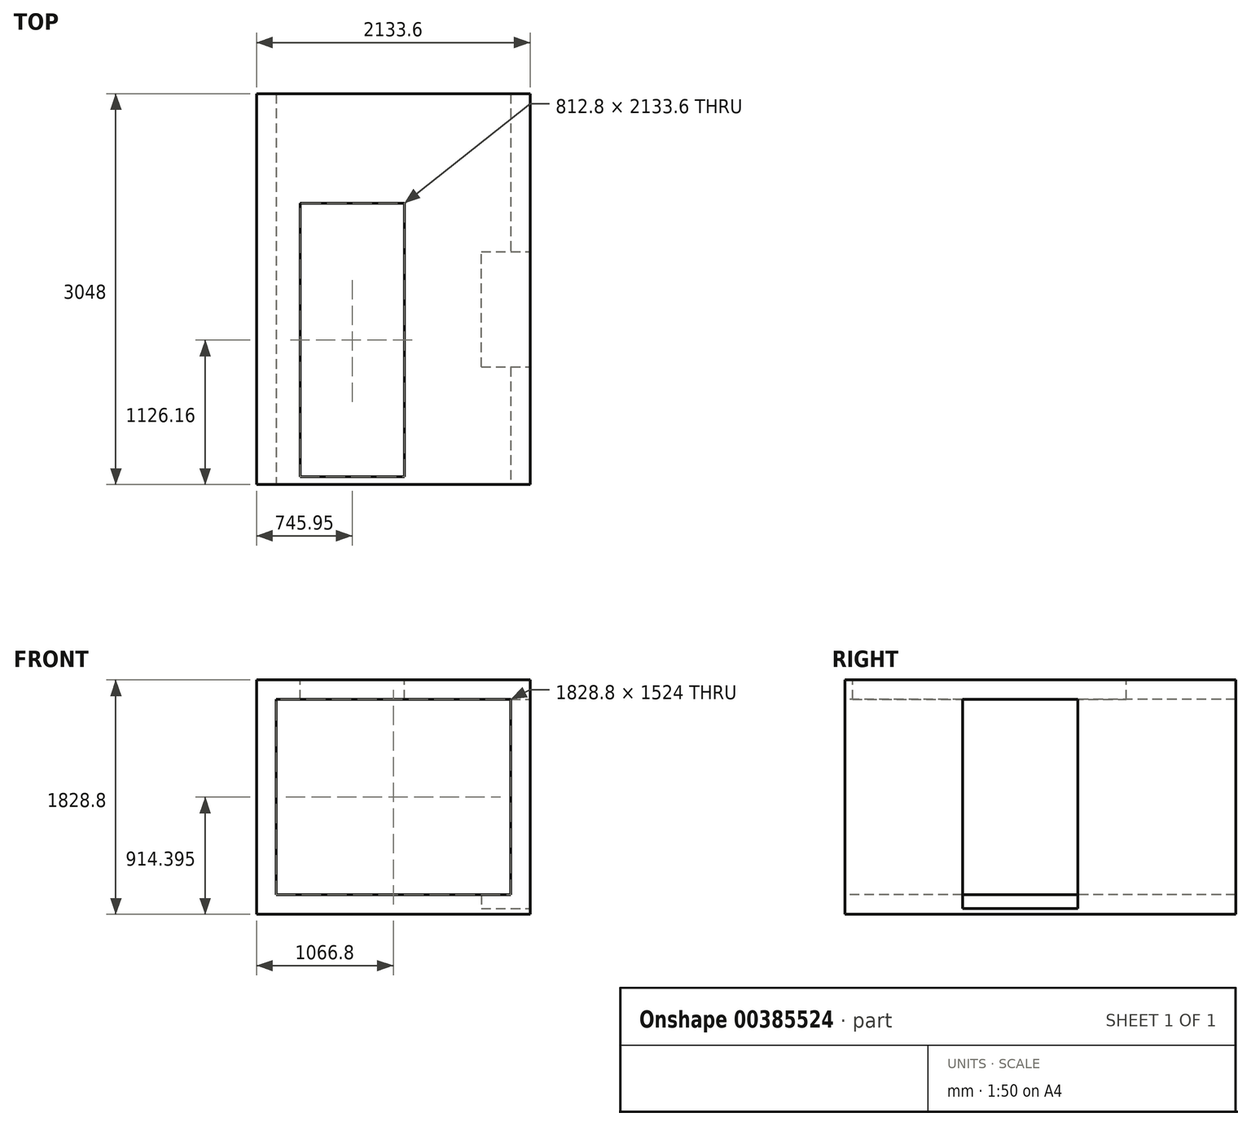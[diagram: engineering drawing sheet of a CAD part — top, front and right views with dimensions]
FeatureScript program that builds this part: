
annotation { "Feature Type Name" : "Feature", "Feature Type Description" : "" }
export const myFeature = defineFeature(function(context is Context, id is Id, definition is map)
    precondition{}
    {
        {
            var Q0;
            Q0=qCreatedBy(makeId("Front.planeOp"),FACE);
            var sketch = newSketch(context, id + "F0", { "sketchPlane" : qUnion([Q0])});
            skLineSegment(sketch, "E0.bottom", {"start": v(1794.05, -42.21) * mm, "end": v(-339.55, -42.21) * mm});
            skLineSegment(sketch, "E0.top", {"start": v(1794.05, 1786.59) * mm, "end": v(-339.55, 1786.59) * mm});
            skLineSegment(sketch, "E0.left", {"start": v(1794.05, -42.21) * mm, "end": v(1794.05, 1786.59) * mm});
            skLineSegment(sketch, "E0.right", {"start": v(-339.55, -42.21) * mm, "end": v(-339.55, 1786.59) * mm});
            skPoint(sketch, "E0.middle", {"position": v(727.25, 872.19) * mm});
            skSolve(sketch);
        }
        {
            var Q0;
            Q0 = qSketchRegion(id + "F0", true);
            extrude(context, id + "F1", {"entities" : qUnion([Q0]), "depth" : 3048 * mm});
        }
        {
            var Q0;
            Q0=makeQuery(id+"F1.opExtrude","CAP_FACE",FACE,{"disambiguationData":[OSD([sQuery(id+"F0.wireOp",EDGE,"E0.bottom"),sQuery(id+"F0.wireOp",EDGE,"E0.top"),sQuery(id+"F0.wireOp",EDGE,"E0.left"),sQuery(id+"F0.wireOp",EDGE,"E0.right")])],"isStart":false});
            var sketch = newSketch(context, id + "F2", { "sketchPlane" : qUnion([Q0])});
            skLineSegment(sketch, "E1.0", {"start": v(1641.65, 110.19) * mm, "end": v(1641.65, 1634.19) * mm});
            skLineSegment(sketch, "E1.1", {"start": v(-187.15, 110.19) * mm, "end": v(1641.65, 110.19) * mm});
            skLineSegment(sketch, "E1.2", {"start": v(-187.15, 1634.19) * mm, "end": v(-187.15, 110.19) * mm});
            skLineSegment(sketch, "E1.3", {"start": v(1641.65, 1634.19) * mm, "end": v(-187.15, 1634.19) * mm});
            skSolve(sketch);
        }
        {
            var Q0;
            Q0 = qSketchRegion(id + "F2", true);
            extrude(context, id + "F3", {"entities" : qUnion([Q0]), "operationType" : NewBodyOperationType.REMOVE, "oppositeDirection" : true, "depth" : 3302 * mm});
        }
        {
            var Q0;
            Q0=makeQuery(id+"F1.opExtrude","SWEPT_FACE",FACE,{"disambiguationData":[OSD([sQuery(id+"F0.wireOp",EDGE,"E0.top")])]});
            var sketch = newSketch(context, id + "F4", { "sketchPlane" : qUnion([Q0])});
            skLineSegment(sketch, "E2.bottom", {"start": v(0, -2988.64) * mm, "end": v(812.8, -2988.64) * mm});
            skLineSegment(sketch, "E2.top", {"start": v(0, -855.04) * mm, "end": v(812.8, -855.04) * mm});
            skLineSegment(sketch, "E2.left", {"start": v(0, -2988.64) * mm, "end": v(0, -855.04) * mm});
            skLineSegment(sketch, "E2.right", {"start": v(812.8, -2988.64) * mm, "end": v(812.8, -855.04) * mm});
            skPoint(sketch, "E2.middle", {"position": v(406.4, -1921.84) * mm});
            skSolve(sketch);
        }
        {
            var Q0;
            Q0=makeQuery(id+"F4.imprint","IMPRINT",FACE,{"disambiguationData":[TD([[makeQuery(id+"F4.imprint","IMPRINT",EDGE,{"derivedFrom":sQuery(id+"F4.wireOp",EDGE,"E2.bottom")}),1.0]])]});
            extrude(context, id + "F5", {"entities" : qUnion([Q0]), "operationType" : NewBodyOperationType.REMOVE, "oppositeDirection" : true, "depth" : 304.8 * mm});
        }
        {
            var Q0;
            Q0=makeQuery(id+"F1.opExtrude","SWEPT_FACE",FACE,{"disambiguationData":[OSD([sQuery(id+"F0.wireOp",EDGE,"E0.left")])]});
            var sketch = newSketch(context, id + "F6", { "sketchPlane" : qUnion([Q0])});
            skLineSegment(sketch, "E3.bottom", {"start": v(-1232.52, 1636.55) * mm, "end": v(-2130.7, 1636.55) * mm});
            skLineSegment(sketch, "E3.top", {"start": v(-1232.52, 3.33) * mm, "end": v(-2130.7, 3.33) * mm});
            skLineSegment(sketch, "E3.left", {"start": v(-1232.52, 1636.55) * mm, "end": v(-1232.52, 3.33) * mm});
            skLineSegment(sketch, "E3.right", {"start": v(-2130.7, 1636.55) * mm, "end": v(-2130.7, 3.33) * mm});
            skPoint(sketch, "E3.middle", {"position": v(-1681.6, 819.94) * mm});
            skSolve(sketch);
        }
        {
            var Q0;
            Q0=makeQuery(id+"F6.imprint","IMPRINT",FACE,{"disambiguationData":[TD([[makeQuery(id+"F6.imprint","IMPRINT",EDGE,{"derivedFrom":sQuery(id+"F6.wireOp",EDGE,"E3.bottom")}),1.0]])]});
            extrude(context, id + "F7", {"entities" : qUnion([Q0]), "operationType" : NewBodyOperationType.REMOVE, "oppositeDirection" : true, "depth" : 381 * mm});
        }
    });
